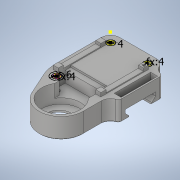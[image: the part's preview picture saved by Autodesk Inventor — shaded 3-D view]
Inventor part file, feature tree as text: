
AUTODESK INVENTOR PART (.ipt)
format: ipt  version: 2021.1 (Build 251245010, 245A)  size: 248,320 bytes
history: mixed  units: in
note: dims shown in document units (in); Inventor stores cm internally (conversion verified against a paired STEP export)
features: extrude x4, direct_edit x3, sketch x3, other x3, chamfer x1, imported_body x1
ambient origin geometry x8: Origin, YZ Plane, XZ Plane, XY Plane, X Axis, Y Axis, Z Axis, Center Point
bodies: Solid1 (imported_parasolid), Body1 (imported_parasolid)
feature tree (15):
  direct_edit  "Direktbearbeitung1"
  direct_edit  "Direktbearbeitung2"
  direct_edit  "Direktbearbeitung3"
  sketch  "Skizze1"  dims[d0=0.1575in d1=0.1575in]
  extrude  "Extrusion1"  Depth=0.1575in
  extrude  "Extrusion2"  Depth=0.2362in
  extrude  "Extrusion3"  Depth=0.0197in TaperAngle=0.0deg
  chamfer  "Fase1"  Distance=0.0197in
  extrude  "Extrusion4"  Depth=0.0197in
  sketch  "Skizze2"  dims[d2=0.1575in d3=0.2362in]
  sketch  "Skizze3"  dims[d4=0.3937in d5=0.0in d6=0.252in d7=0.0in d8=0.0197in d9=0.0197in d10=0.0197in d11=0.0197in d12=0.0in d13=0.0197in d14=0.0787in d15=45.0deg d16=0.2756in d17=0.2362in d18=0.0197in d19=0.0in]
  other  "Löschen1"
  other  "Löschen2"
  other  "Löschen3"
  imported_body  NMx_Import_Brep_tag  [imported B-rep: ~123 faces, bbox_mm=[34.6, 13.0, 51.0]]
